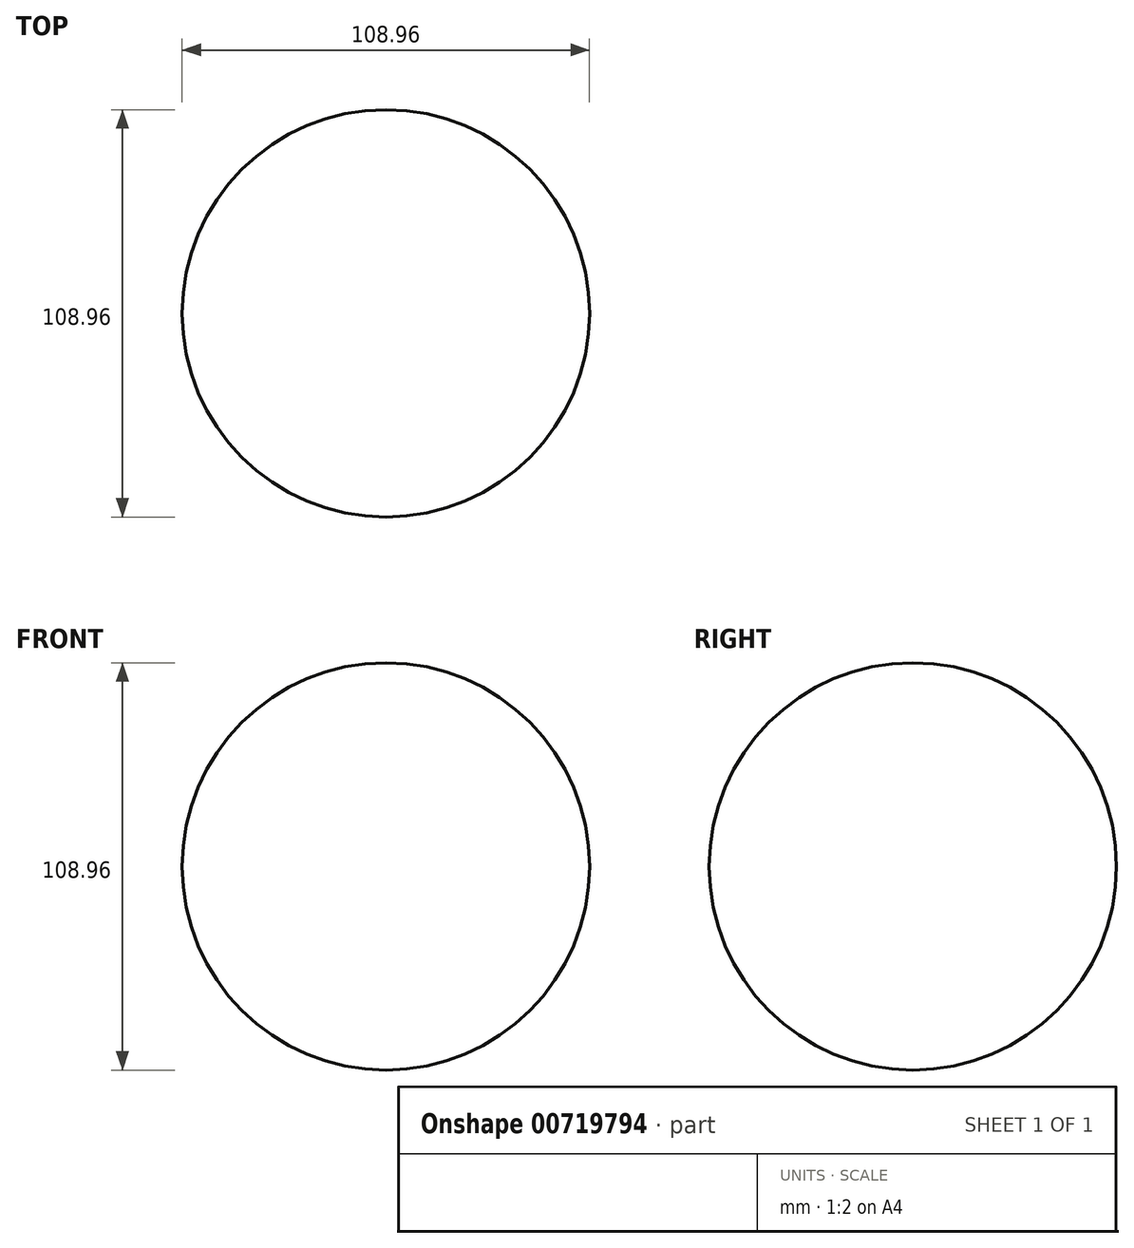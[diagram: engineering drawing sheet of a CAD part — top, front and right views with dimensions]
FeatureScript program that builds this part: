
annotation { "Feature Type Name" : "Feature", "Feature Type Description" : "" }
export const myFeature = defineFeature(function(context is Context, id is Id, definition is map)
    precondition{}
    {
        {
            var Q0;
            Q0=qCreatedBy(makeId("Front.planeOp"),FACE);
            var sketch = newSketch(context, id + "F0", { "sketchPlane" : qUnion([Q0])});
            skArc(sketch, "E0", {"start": v(54.48, 0) * mm, "mid": v(0, 54.48) * mm, "end": v(-54.48, 0) * mm});
            skLineSegment(sketch, "E1", {"start": v(-54.48, 0) * mm, "end": v(54.48, 0) * mm});
            skSolve(sketch);
        }
        {
            var Q0;
            Q0=sQuery(id+"F0.wireOp",EDGE,"E0");
            var Q1;
            Q1=sQuery(id+"F0.wireOp",EDGE,"E1");
            revolve(context, id + "F1", {"bodyType" : ToolBodyType.SURFACE, "operationType" : NewBodyOperationType.INTERSECT, "surfaceOperationType" : NewSurfaceOperationType.NEW, "surfaceEntities" : qUnion([Q0]), "axis" : qUnion([Q1]), "revolveType" : RevolveType.FULL});
        }
    });
